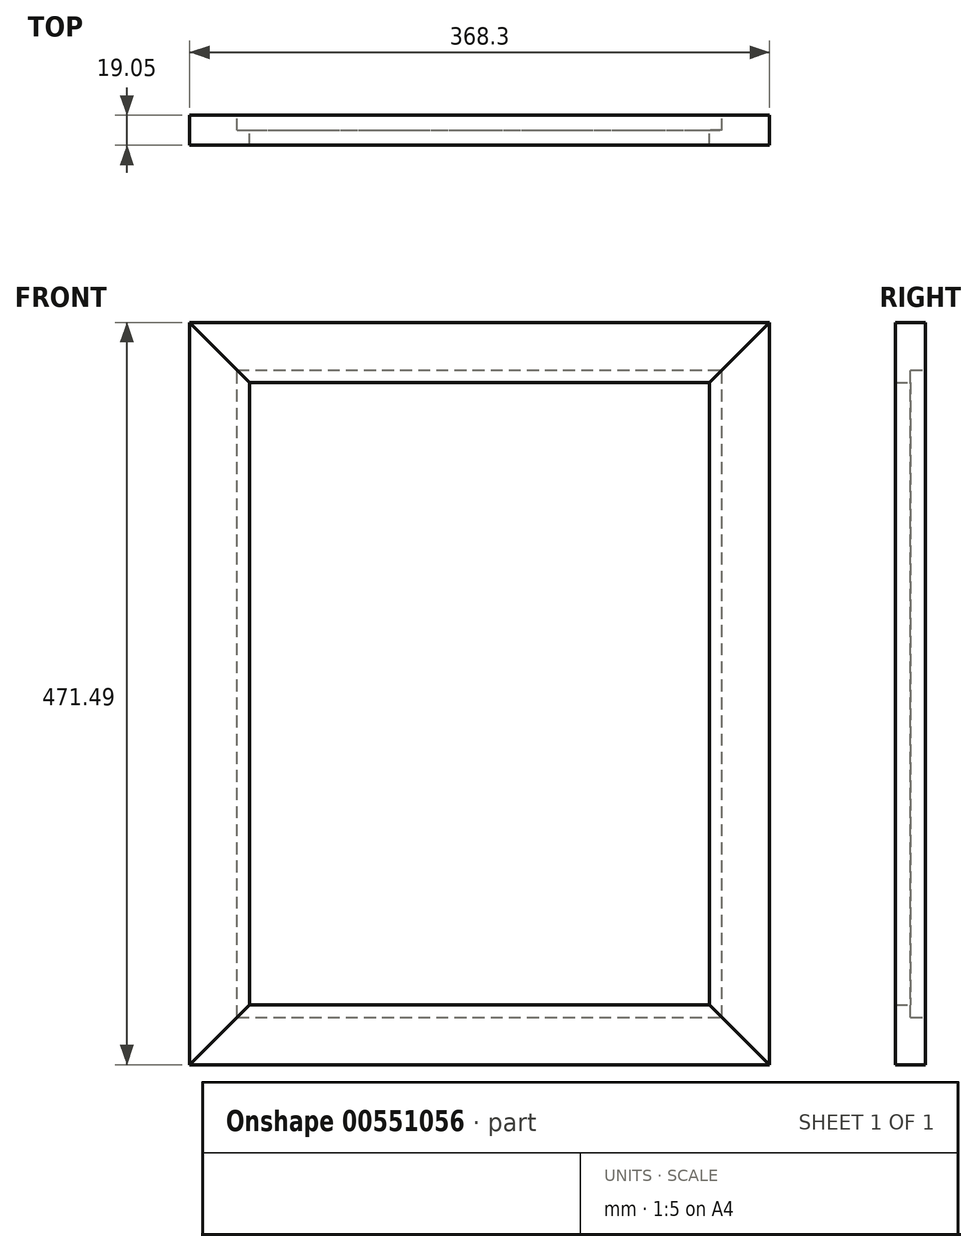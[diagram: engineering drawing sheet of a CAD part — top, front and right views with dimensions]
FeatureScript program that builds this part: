
annotation { "Feature Type Name" : "Feature", "Feature Type Description" : "" }
export const myFeature = defineFeature(function(context is Context, id is Id, definition is map)
    precondition{}
    {
        {
            var Q0;
            Q0=qCreatedBy(makeId("Front.planeOp"),FACE);
            var sketch = newSketch(context, id + "F0", { "sketchPlane" : qUnion([Q0])});
            skLineSegment(sketch, "E0", {"start": v(0, 0) * mm, "end": v(0, 471.49) * mm});
            skLineSegment(sketch, "E1", {"start": v(0, 471.49) * mm, "end": v(-38.1, 433.39) * mm});
            skLineSegment(sketch, "E2", {"start": v(-38.1, 433.39) * mm, "end": v(-38.1, 38.1) * mm});
            skLineSegment(sketch, "E3", {"start": v(-38.1, 38.1) * mm, "end": v(0, 0) * mm});
            skLineSegment(sketch, "E4", {"start": v(-38.1, 433.39) * mm, "end": v(-330.2, 433.39) * mm});
            skLineSegment(sketch, "E5", {"start": v(-330.2, 433.39) * mm, "end": v(-330.2, 38.1) * mm});
            skLineSegment(sketch, "E6", {"start": v(-330.2, 38.1) * mm, "end": v(-38.1, 38.1) * mm});
            skLineSegment(sketch, "E7", {"start": v(0, 471.49) * mm, "end": v(-368.3, 471.49) * mm});
            skLineSegment(sketch, "E8", {"start": v(-368.3, 471.49) * mm, "end": v(-368.3, 0) * mm});
            skLineSegment(sketch, "E9", {"start": v(-368.3, 0) * mm, "end": v(0, 0) * mm});
            skLineSegment(sketch, "E10", {"start": v(-330.2, 38.1) * mm, "end": v(-368.3, 0) * mm});
            skLineSegment(sketch, "E11", {"start": v(-330.2, 433.39) * mm, "end": v(-368.3, 471.49) * mm});
            skSolve(sketch);
        }
        {
            var Q0;
            Q0=makeQuery(id+"F0.imprint","IMPRINT",FACE,{"disambiguationData":[TD([[makeQuery(id+"F0.imprint","IMPRINT",EDGE,{"derivedFrom":sQuery(id+"F0.wireOp",EDGE,"E0")}),1.0]])]});
            extrude(context, id + "F1", {"entities" : qUnion([Q0]), "depth" : 19.05 * mm, "offsetDistance" : 25.4 * mm});
        }
        {
            var Q0;
            Q0=makeQuery(id+"F0.imprint","IMPRINT",FACE,{"disambiguationData":[TD([[makeQuery(id+"F0.imprint","IMPRINT",EDGE,{"derivedFrom":sQuery(id+"F0.wireOp",EDGE,"E1")}),-1.0]])]});
            extrude(context, id + "F2", {"entities" : qUnion([Q0]), "depth" : 19.05 * mm, "offsetDistance" : 25.4 * mm});
        }
        {
            var Q0;
            Q0=makeQuery(id+"F0.imprint","IMPRINT",FACE,{"disambiguationData":[TD([[makeQuery(id+"F0.imprint","IMPRINT",EDGE,{"derivedFrom":sQuery(id+"F0.wireOp",EDGE,"E5")}),-1.0]])]});
            extrude(context, id + "F3", {"entities" : qUnion([Q0]), "depth" : 19.05 * mm, "offsetDistance" : 25.4 * mm});
        }
        {
            var Q0;
            Q0=makeQuery(id+"F0.imprint","IMPRINT",FACE,{"disambiguationData":[TD([[makeQuery(id+"F0.imprint","IMPRINT",EDGE,{"derivedFrom":sQuery(id+"F0.wireOp",EDGE,"E3")}),-1.0]])]});
            extrude(context, id + "F4", {"entities" : qUnion([Q0]), "depth" : 19.05 * mm, "offsetDistance" : 25.4 * mm});
        }
        {
            var Q0;
            Q0=makeQuery(id+"F2.opExtrude","CAP_FACE",FACE,{"disambiguationData":[OSD([sQuery(id+"F0.wireOp",EDGE,"E1"),sQuery(id+"F0.wireOp",EDGE,"E4"),sQuery(id+"F0.wireOp",EDGE,"E7"),sQuery(id+"F0.wireOp",EDGE,"E11")])],"isStart":true});
            var sketch = newSketch(context, id + "F5", { "sketchPlane" : qUnion([Q0])});
            skLineSegment(sketch, "E12.bottom", {"start": v(338.14, 30.16) * mm, "end": v(30.16, 30.16) * mm});
            skLineSegment(sketch, "E12.top", {"start": v(338.14, 441.33) * mm, "end": v(30.16, 441.33) * mm});
            skLineSegment(sketch, "E12.left", {"start": v(338.14, 30.16) * mm, "end": v(338.14, 441.33) * mm});
            skLineSegment(sketch, "E12.right", {"start": v(30.16, 30.16) * mm, "end": v(30.16, 441.33) * mm});
            skPoint(sketch, "E13", {"position": v(184.15, 441.33) * mm});
            skPoint(sketch, "E14", {"position": v(30.16, 235.74) * mm});
            skLineSegment(sketch, "E15.0", {"start": v(0, 0) * mm, "end": v(0, 471.49) * mm});
            skPoint(sketch, "E16.0", {"position": v(184.15, 471.49) * mm});
            skPoint(sketch, "E17.0", {"position": v(368.3, 235.74) * mm});
            skPoint(sketch, "E18.0", {"position": v(38.1, 235.74) * mm});
            skPoint(sketch, "E19.0", {"position": v(184.15, 433.39) * mm});
            skLineSegment(sketch, "E20.0", {"start": v(330.2, 38.1) * mm, "end": v(38.1, 38.1) * mm});
            skLineSegment(sketch, "E21.0", {"start": v(330.2, 433.39) * mm, "end": v(330.2, 38.1) * mm});
            skLineSegment(sketch, "E22.0", {"start": v(38.1, 433.39) * mm, "end": v(330.2, 433.39) * mm});
            skLineSegment(sketch, "E23.0", {"start": v(38.1, 433.39) * mm, "end": v(38.1, 38.1) * mm});
            skLineSegment(sketch, "E24.top", {"start": v(38.1, 38.1) * mm, "end": v(330.2, 38.1) * mm});
            skSolve(sketch);
        }
        {
            var Q0;
            Q0=makeQuery(id+"F5.imprint","IMPRINT",FACE,{"disambiguationData":[TD([[makeQuery(id+"F5.imprint","IMPRINT",EDGE,{"derivedFrom":sQuery(id+"F5.wireOp",EDGE,"E12.bottom")}),-1.0]])]});
            var Q1;
            {var subQ0=sQuery(id+"F5.wireOp",EDGE,"E12.top");Q1=makeQuery(id+"F5.imprint","IMPRINT",FACE,{"disambiguationData":[TD([[makeQuery(id+"F5.imprint","IMPRINT",EDGE,{"derivedFrom":subQ0}),1.0]])]});}
            extrude(context, id + "F6", {"entities" : qUnion([Q0, Q1]), "operationType" : NewBodyOperationType.REMOVE, "oppositeDirection" : true, "depth" : 9.52 * mm, "offsetDistance" : 25.4 * mm});
        }
    });
